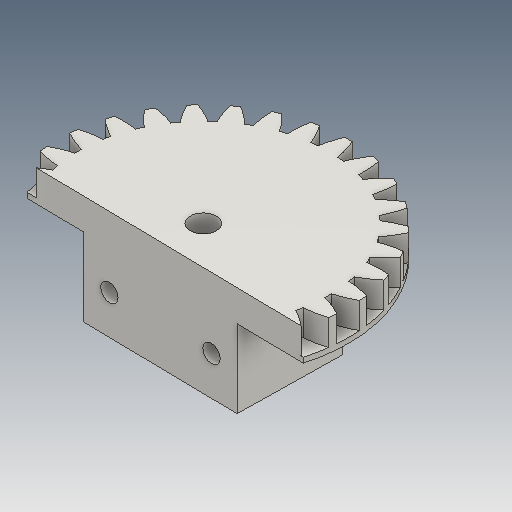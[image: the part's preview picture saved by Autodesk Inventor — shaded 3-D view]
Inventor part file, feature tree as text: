
AUTODESK INVENTOR PART (.ipt)
format: ipt  version: 2018 (Build 220112000, 112)  size: 291,840 bytes
history: native  units: mm
features: other x13, sketch x9, plane x4
ambient origin geometry x8: Origin, YZ Plane, XZ Plane, XY Plane, X Axis, Y Axis, Z Axis, Center Point
bodies: Volumenkörper1 (feature_tree)
feature tree (26):
  other  "Stirnzahnrad1"
  other  "Solid1::Stirnzahnrad1"
  other  "Bezeichnung1"
  sketch  "Sketch1"  dims[d0=10.0mm]
  sketch  "Sketch2"  dims[d16=40.0mm d17=0.0mm d41=0.0mm d43=40.0mm d46=40.0mm d47=0.0mm d48=0.0mm]
  sketch  "Skizze9"
  sketch  "Skizze10"
  sketch  "Skizze11"
  sketch  "Skizze12"
  sketch  "Skizze13"
  sketch  "Skizze14"
  sketch  "Skizze15"
  plane  "XZ Plane_1"
  plane  "Work Plane2"
  plane  "Work Plane8"
  plane  "Work Plane9"
  other  "Z Axis_1"
  other  "Flä1"
  other  "Srf1::Abgeleitet"
  other  "Abstands-iMate"
  other  "Ausrichtungs-iMate"
  other  "Netz-iMate"
  other  "Achsen-iMate"
  other  "Positions-iMate"
  other  "Netz-iMate 2"
  other  "Startebenen-iMate"
